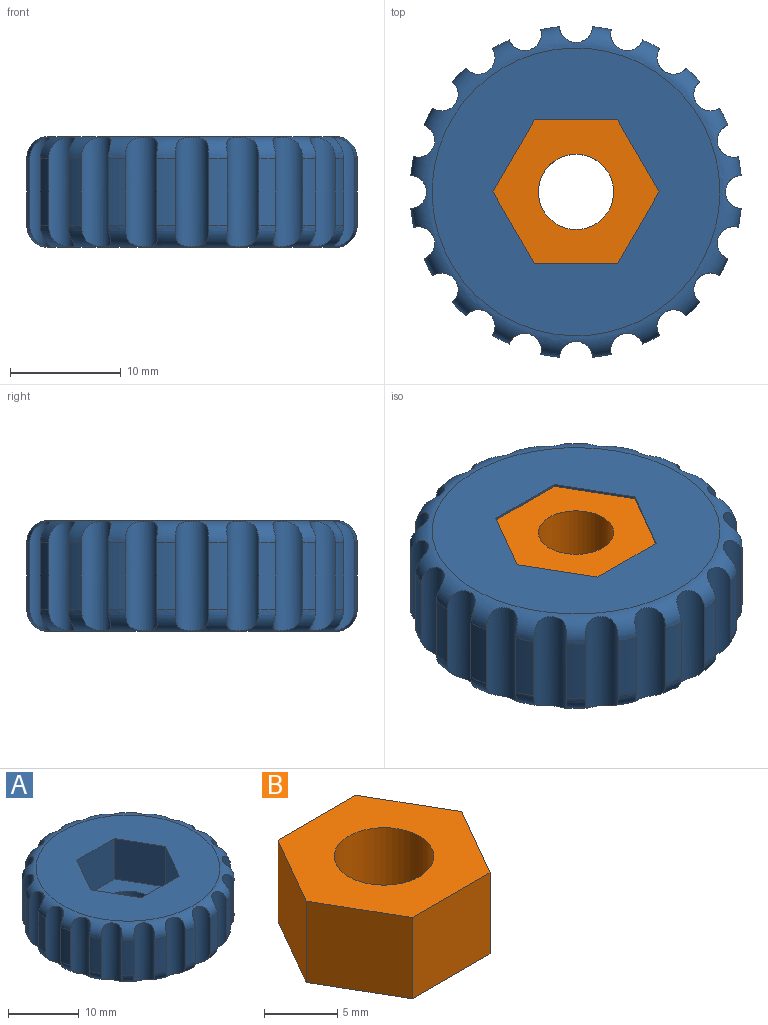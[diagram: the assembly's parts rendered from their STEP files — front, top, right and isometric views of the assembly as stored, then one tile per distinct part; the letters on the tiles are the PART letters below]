
ASSEMBLY  parts=2 mates=1
PART A: 52 faces, bbox 32.5x32.5x10 mm
  f0: cylinder r=15mm len=6mm, axis (0,0,-1), area 10.3mm2, adj f30,f31,f35,f51
  f1: cylinder r=15mm len=6mm, axis (0,0,-1), area 10.3mm2, adj f30,f31,f50,f51
  f2: cylinder r=15mm len=6mm, axis (0,0,-1), area 10.3mm2, adj f30,f31,f49,f50
  f3: cylinder r=15mm len=6mm, axis (0,0,-1), area 10.3mm2, adj f30,f31,f48,f49
  f4: cylinder r=15mm len=6mm, axis (0,0,-1), area 10.3mm2, adj f30,f31,f47,f48
  f5: cylinder r=15mm len=6mm, axis (0,0,-1), area 10.3mm2, adj f30,f31,f46,f47
  f6: cylinder r=15mm len=6mm, axis (0,0,-1), area 10.3mm2, adj f30,f31,f45,f46
  f7: cylinder r=15mm len=6mm, axis (0,0,-1), area 10.3mm2, adj f30,f31,f43,f44
  f8: cylinder r=15mm len=6mm, axis (0,0,-1), area 10.3mm2, adj f30,f31,f43,f45
  f9: cylinder r=15mm len=6mm, axis (0,0,-1), area 10.3mm2, adj f30,f31,f42,f44
  f10: cylinder r=15mm len=6mm, axis (0,0,-1), area 10.3mm2, adj f30,f31,f41,f42
  f11: cylinder r=15mm len=6mm, axis (0,0,-1), area 10.3mm2, adj f30,f31,f40,f41
  f12: cylinder r=15mm len=6mm, axis (0,0,-1), area 10.3mm2, adj f30,f31,f39,f40
  f13: cylinder r=15mm len=6mm, axis (0,0,-1), area 10.3mm2, adj f30,f31,f38,f39
  f14: cylinder r=15mm len=6mm, axis (0,0,-1), area 10.3mm2, adj f30,f31,f37,f38
  f15: cylinder r=15mm len=6mm, axis (0,0,-1), area 10.3mm2, adj f30,f31,f36,f37
  f16: cylinder r=15mm len=6mm, axis (0,0,-1), area 10.3mm2, adj f30,f31,f34,f35
  f17: cylinder r=15mm len=6mm, axis (0,0,-1), area 10.3mm2, adj f30,f31,f33,f34
  f18: cylinder r=15mm len=6mm, axis (0,0,-1), area 10.3mm2, adj f30,f31,f32,f33
  f19: cylinder r=4.25mm len=8.5mm, axis (0,0,-1), area 80.1mm2, adj f22,f29
  f20: cylinder r=15mm len=6mm, axis (0,0,-1), area 10.3mm2, adj f30,f31,f32,f36
  f21: plane 26x26mm, normal (0,0,1), area 384.6mm2, adj f23,f24,f25,f26,f27,f28,f31
  f22: plane 26x26mm, normal (0,0,-1), area 474.2mm2, adj f19,f30
  f23: plane 7x6.5mm, normal (0.87,0.5,0), area 52.5mm2, adj f21,f24,f28,f29
  f24: plane 7.51x7mm, normal (0,1,0), area 52.5mm2, adj f21,f23,f25,f29
  f25: plane 7x6.5mm, normal (-0.87,0.5,0), area 52.5mm2, adj f21,f24,f26,f29
  f26: plane 7x6.5mm, normal (-0.87,-0.5,0), area 52.5mm2, adj f21,f25,f27,f29
  f27: plane 7.51x7mm, normal (0,-1,0), area 52.5mm2, adj f21,f26,f28,f29
  f28: plane 7x6.5mm, normal (0.87,-0.5,0), area 52.5mm2, adj f21,f23,f27,f29
  f29: plane 15.01x13mm, normal (0,0,1), area 89.6mm2, adj f19,f23,f24,f25,f26,f27,f28
  f30: torus R=13mm, axis (0,0,1), area 147.4mm2, adj f0,f1,f2,f3,f4,f5,f6,f7
  f31: torus R=13mm, axis (0,0,1), area 147.4mm2, adj f0,f1,f2,f3,f4,f5,f6,f7
  f32: cylinder r=1.5mm len=9.87mm, axis (0,0,1), area 41.8mm2, adj f18,f20,f30,f31
  f33: cylinder r=1.5mm len=9.87mm, axis (0,0,1), area 41.8mm2, adj f17,f18,f30,f31
  f34: cylinder r=1.5mm len=9.87mm, axis (0,0,1), area 41.8mm2, adj f16,f17,f30,f31
  f35: cylinder r=1.5mm len=9.87mm, axis (0,0,1), area 41.8mm2, adj f0,f16,f30,f31
  f36: cylinder r=1.5mm len=9.87mm, axis (0,0,1), area 41.8mm2, adj f15,f20,f30,f31
  f37: cylinder r=1.5mm len=9.87mm, axis (0,0,1), area 41.8mm2, adj f14,f15,f30,f31
  f38: cylinder r=1.5mm len=9.87mm, axis (0,0,1), area 41.8mm2, adj f13,f14,f30,f31
  f39: cylinder r=1.5mm len=9.87mm, axis (0,0,1), area 41.8mm2, adj f12,f13,f30,f31
  f40: cylinder r=1.5mm len=9.87mm, axis (0,0,1), area 41.8mm2, adj f11,f12,f30,f31
  f41: cylinder r=1.5mm len=9.87mm, axis (0,0,1), area 41.8mm2, adj f10,f11,f30,f31
  f42: cylinder r=1.5mm len=9.87mm, axis (0,0,1), area 41.8mm2, adj f9,f10,f30,f31
  f43: cylinder r=1.5mm len=9.87mm, axis (0,0,1), area 41.8mm2, adj f7,f8,f30,f31
  f44: cylinder r=1.5mm len=9.87mm, axis (0,0,1), area 41.8mm2, adj f7,f9,f30,f31
  f45: cylinder r=1.5mm len=9.87mm, axis (0,0,1), area 41.8mm2, adj f6,f8,f30,f31
  f46: cylinder r=1.5mm len=9.87mm, axis (0,0,1), area 41.8mm2, adj f5,f6,f30,f31
  f47: cylinder r=1.5mm len=9.87mm, axis (0,0,1), area 41.8mm2, adj f4,f5,f30,f31
  f48: cylinder r=1.5mm len=9.87mm, axis (0,0,1), area 41.8mm2, adj f3,f4,f30,f31
  f49: cylinder r=1.5mm len=9.87mm, axis (0,0,1), area 41.8mm2, adj f2,f3,f30,f31
  f50: cylinder r=1.5mm len=9.87mm, axis (0,0,1), area 41.8mm2, adj f1,f2,f30,f31
  f51: cylinder r=1.5mm len=9.87mm, axis (0,0,1), area 41.8mm2, adj f0,f1,f30,f31
PART B: 9 faces, bbox 15x13x6.8 mm
  f0: plane 6.8x6.5mm, normal (-0.87,-0.5,0), area 51mm2, adj f1,f6,f7,f8
  f1: plane 7.51x6.8mm, normal (0,-1,0), area 51mm2, adj f0,f2,f7,f8
  f2: plane 6.8x6.5mm, normal (0.87,-0.5,0), area 51mm2, adj f1,f3,f7,f8
  f3: plane 6.8x6.5mm, normal (0.87,0.5,0), area 51mm2, adj f2,f4,f7,f8
  f4: plane 7.51x6.8mm, normal (0,1,0), area 51mm2, adj f3,f6,f7,f8
  f5: cylinder r=3.4mm len=6.8mm, axis (0,0,-1), area 145.3mm2, adj f7,f8
  f6: plane 6.8x6.5mm, normal (-0.87,0.5,0), area 51mm2, adj f0,f4,f7,f8
  f7: plane 15.01x13mm, normal (0,0,1), area 110mm2, adj f0,f1,f2,f3,f4,f5,f6
  f8: plane 15.01x13mm, normal (0,0,-1), area 110mm2, adj f0,f1,f2,f3,f4,f5,f6
PLACE A t=(11.01,18.15,11.28)mm
PLACE B t=(11.01,18.15,14.28)mm fixed
MATE fastened A.f19 <-> B.f5  axis (0,0,1) through (11.01,18.15,14.28)mm
